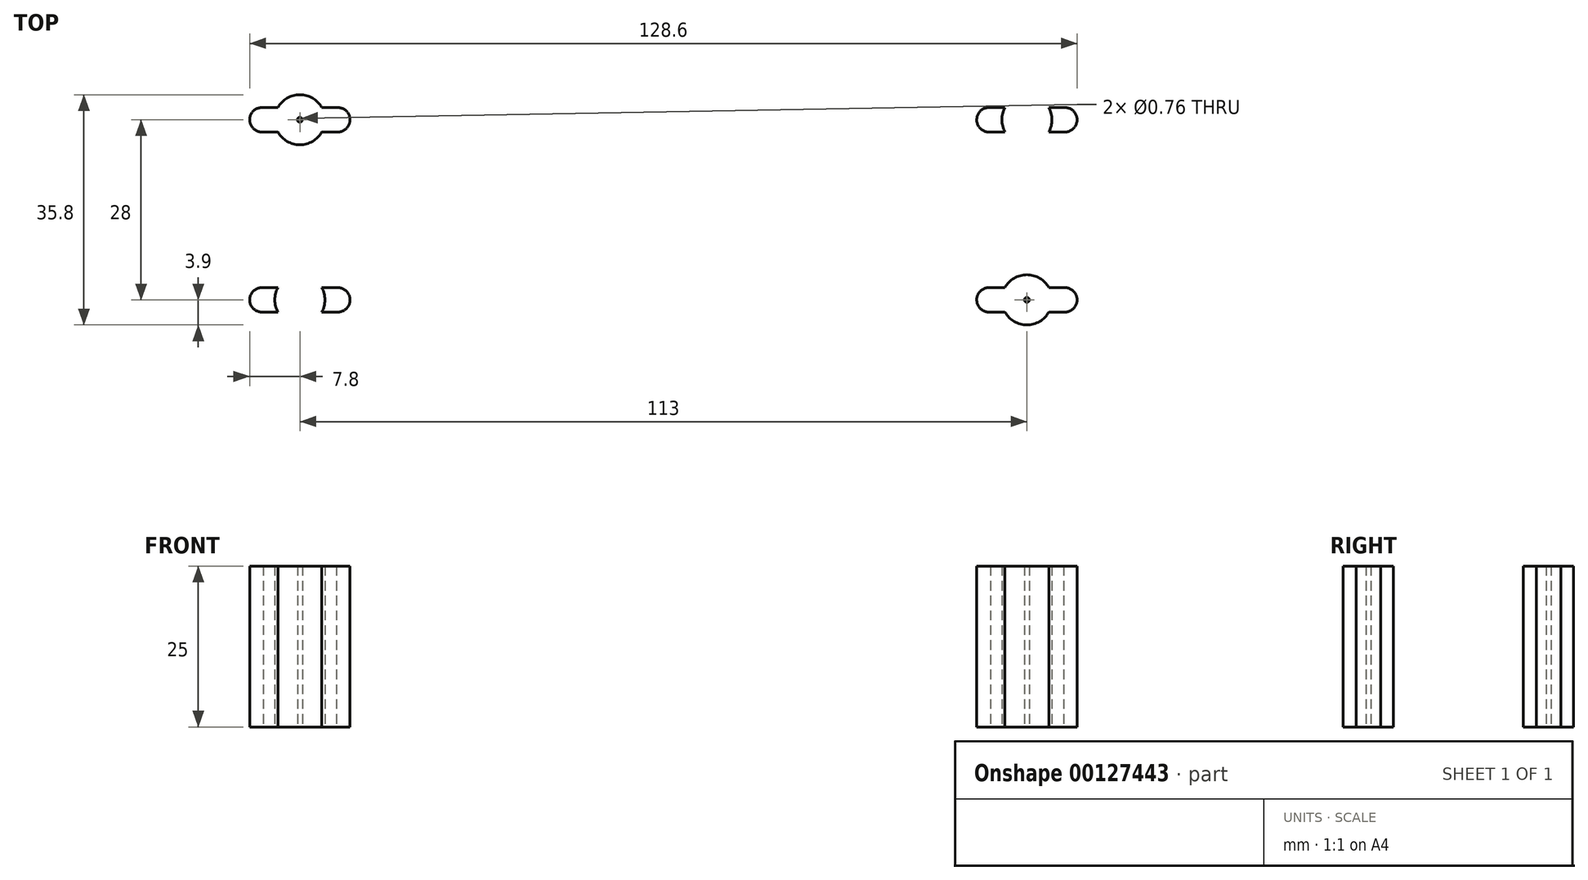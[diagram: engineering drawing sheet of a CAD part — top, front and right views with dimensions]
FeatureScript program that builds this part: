
annotation { "Feature Type Name" : "Feature", "Feature Type Description" : "" }
export const myFeature = defineFeature(function(context is Context, id is Id, definition is map)
    precondition{}
    {
        {
            var Q0;
            Q0=qCreatedBy(makeId("Top.planeOp"),FACE);
            var sketch = newSketch(context, id + "F0", { "sketchPlane" : qUnion([Q0])});
            skLineSegment(sketch, "E0", {"start": v(-53.1, 15.9) * mm, "end": v(-50.6, 15.9) * mm});
            skLineSegment(sketch, "E1", {"start": v(-53.1, 12.1) * mm, "end": v(-50.81, 12.1) * mm});
            skArc(sketch, "E2", {"start": v(-50.6, 15.9) * mm, "mid": v(-48.7, 13.9) * mm, "end": v(-50.81, 12.1) * mm});
            skLineSegment(sketch, "E3", {"start": v(-56.5, 10.1) * mm, "end": v(-56.5, 17.9) * mm, "construction": true});
            skLineSegment(sketch, "E4.MirrorCS", {"start": v(-59.9, 15.9) * mm, "end": v(-62.4, 15.9) * mm});
            skArc(sketch, "E5.MirrorCS", {"start": v(-62.4, 15.9) * mm, "mid": v(-64.3, 13.9) * mm, "end": v(-62.19, 12.1) * mm});
            skLineSegment(sketch, "E6.MirrorCS", {"start": v(-59.9, 12.1) * mm, "end": v(-62.19, 12.1) * mm});
            skArc(sketch, "E7", {"start": v(-59.9, 12.1) * mm, "mid": v(-56.5, 10.1) * mm, "end": v(-53.1, 12.1) * mm});
            skLineSegment(sketch, "E8", {"start": v(0, 35.13) * mm, "end": v(0, -25.28) * mm, "construction": true});
            skLineSegment(sketch, "E9", {"start": v(-57.6, 0) * mm, "end": v(-1, 0) * mm, "construction": true});
            skLineSegment(sketch, "E10.MirrorCS", {"start": v(53.1, 15.9) * mm, "end": v(50.6, 15.9) * mm});
            skLineSegment(sketch, "E11.MirrorCS", {"start": v(53.1, 12.1) * mm, "end": v(50.81, 12.1) * mm});
            skLineSegment(sketch, "E12.MirrorCS", {"start": v(59.9, 12.1) * mm, "end": v(62.19, 12.1) * mm});
            skLineSegment(sketch, "E13.MirrorCS", {"start": v(59.9, 15.9) * mm, "end": v(62.4, 15.9) * mm});
            skArc(sketch, "E14.MirrorCS", {"start": v(50.6, 15.9) * mm, "mid": v(48.7, 13.9) * mm, "end": v(50.81, 12.1) * mm});
            skArc(sketch, "E15.MirrorCS", {"start": v(62.4, 15.9) * mm, "mid": v(64.3, 13.9) * mm, "end": v(62.19, 12.1) * mm});
            skCircle(sketch, "E16.MirrorC", {"center": v(56.5, 14) * mm, "radius": 3.9 * mm});
            skLineSegment(sketch, "E17.MirrorCS", {"start": v(56.5, 10.1) * mm, "end": v(56.5, 17.9) * mm, "construction": true});
            skLineSegment(sketch, "E18.MirrorCS", {"start": v(53.1, -12.1) * mm, "end": v(50.81, -12.1) * mm});
            skLineSegment(sketch, "E19.MirrorCS", {"start": v(53.1, -15.9) * mm, "end": v(50.6, -15.9) * mm});
            skLineSegment(sketch, "E20.MirrorCS", {"start": v(59.9, -12.1) * mm, "end": v(62.19, -12.1) * mm});
            skLineSegment(sketch, "E21.MirrorCS", {"start": v(59.9, -15.9) * mm, "end": v(62.4, -15.9) * mm});
            skLineSegment(sketch, "E22.MirrorCS", {"start": v(-59.9, -12.1) * mm, "end": v(-62.19, -12.1) * mm});
            skCircle(sketch, "E23.MirrorC", {"center": v(56.5, -14) * mm, "radius": 3.9 * mm});
            skLineSegment(sketch, "E24.MirrorCS", {"start": v(-53.1, -12.1) * mm, "end": v(-50.81, -12.1) * mm});
            skLineSegment(sketch, "E25.MirrorCS", {"start": v(56.5, -10.1) * mm, "end": v(56.5, -17.9) * mm, "construction": true});
            skLineSegment(sketch, "E26.MirrorCS", {"start": v(-56.5, -10.1) * mm, "end": v(-56.5, -17.9) * mm, "construction": true});
            skLineSegment(sketch, "E27.MirrorCS", {"start": v(-53.1, -15.9) * mm, "end": v(-50.6, -15.9) * mm});
            skLineSegment(sketch, "E28.MirrorCS", {"start": v(-59.9, -15.9) * mm, "end": v(-62.4, -15.9) * mm});
            skCircle(sketch, "E29.MirrorC", {"center": v(-56.5, -14) * mm, "radius": 3.9 * mm});
            skArc(sketch, "E30.MirrorCS", {"start": v(-50.6, -15.9) * mm, "mid": v(-48.7, -13.9) * mm, "end": v(-50.81, -12.1) * mm});
            skArc(sketch, "E31.MirrorCS", {"start": v(62.4, -15.9) * mm, "mid": v(64.3, -13.9) * mm, "end": v(62.19, -12.1) * mm});
            skArc(sketch, "E32.MirrorCS", {"start": v(-62.4, -15.9) * mm, "mid": v(-64.3, -13.9) * mm, "end": v(-62.19, -12.1) * mm});
            skArc(sketch, "E33.MirrorCS", {"start": v(50.6, -15.9) * mm, "mid": v(48.7, -13.9) * mm, "end": v(50.81, -12.1) * mm});
            skArc(sketch, "E34.trimOffspring", {"start": v(-53.1, 15.9) * mm, "mid": v(-56.5, 17.9) * mm, "end": v(-59.9, 15.9) * mm});
            skCircle(sketch, "E35", {"center": v(-56.5, 14) * mm, "radius": 0.38 * mm});
            skCircle(sketch, "E36.MirrorC", {"center": v(-56.5, -14) * mm, "radius": 0.38 * mm});
            skCircle(sketch, "E37.MirrorC", {"center": v(56.5, 14) * mm, "radius": 0.38 * mm});
            skCircle(sketch, "E38.MirrorC", {"center": v(56.5, -14) * mm, "radius": 0.38 * mm});
            skSolve(sketch);
        }
        {
            var Q0;
            Q0=makeQuery(id+"F0.imprint","IMPRINT",FACE,{"disambiguationData":[TD([[makeQuery(id+"F0.imprint","IMPRINT",EDGE,{"derivedFrom":sQuery(id+"F0.wireOp",EDGE,"E0")}),-1.0]])]});
            var Q1;
            {var subQ0=sQuery(id+"F0.wireOp",EDGE,"E29.MirrorC");var subQ1=makeQuery(id+"F0.imprint","INTERSECT",VERTEX,{"derivedFrom":[sQuery(id+"F0.wireOp",EDGE,"E27.MirrorCS"),subQ0]});Q1=makeQuery(id+"F0.imprint","IMPRINT",FACE,{"disambiguationData":[TD([[makeQuery(id+"F0.imprint","IMPRINT",EDGE,{"disambiguationData":[TD([[subQ1,-1.0]])],"derivedFrom":subQ0}),-1.0]])]});}
            var Q2;
            {var subQ0=sQuery(id+"F0.wireOp",EDGE,"E24.MirrorCS");Q2=makeQuery(id+"F0.imprint","IMPRINT",FACE,{"disambiguationData":[TD([[makeQuery(id+"F0.imprint","IMPRINT",EDGE,{"derivedFrom":subQ0}),-1.0]])]});}
            var Q3;
            {var subQ0=sQuery(id+"F0.wireOp",EDGE,"E22.MirrorCS");Q3=makeQuery(id+"F0.imprint","IMPRINT",FACE,{"disambiguationData":[TD([[makeQuery(id+"F0.imprint","IMPRINT",EDGE,{"derivedFrom":subQ0}),1.0]])]});}
            var Q4;
            {var subQ0=sQuery(id+"F0.wireOp",EDGE,"E18.MirrorCS");Q4=makeQuery(id+"F0.imprint","IMPRINT",FACE,{"disambiguationData":[TD([[makeQuery(id+"F0.imprint","IMPRINT",EDGE,{"derivedFrom":subQ0}),1.0]])]});}
            var Q5;
            {var subQ0=sQuery(id+"F0.wireOp",EDGE,"E23.MirrorC");var subQ1=makeQuery(id+"F0.imprint","INTERSECT",VERTEX,{"derivedFrom":[sQuery(id+"F0.wireOp",EDGE,"E19.MirrorCS"),subQ0]});Q5=makeQuery(id+"F0.imprint","IMPRINT",FACE,{"disambiguationData":[TD([[makeQuery(id+"F0.imprint","IMPRINT",EDGE,{"disambiguationData":[TD([[subQ1,-1.0]])],"derivedFrom":subQ0}),1.0]])]});}
            var Q6;
            {var subQ0=sQuery(id+"F0.wireOp",EDGE,"E20.MirrorCS");Q6=makeQuery(id+"F0.imprint","IMPRINT",FACE,{"disambiguationData":[TD([[makeQuery(id+"F0.imprint","IMPRINT",EDGE,{"derivedFrom":subQ0}),-1.0]])]});}
            var Q7;
            {var subQ0=sQuery(id+"F0.wireOp",EDGE,"E12.MirrorCS");Q7=makeQuery(id+"F0.imprint","IMPRINT",FACE,{"disambiguationData":[TD([[makeQuery(id+"F0.imprint","IMPRINT",EDGE,{"derivedFrom":subQ0}),1.0]])]});}
            var Q8;
            {var subQ0=sQuery(id+"F0.wireOp",EDGE,"E16.MirrorC");var subQ1=makeQuery(id+"F0.imprint","INTERSECT",VERTEX,{"derivedFrom":[sQuery(id+"F0.wireOp",EDGE,"E10.MirrorCS"),subQ0]});Q8=makeQuery(id+"F0.imprint","IMPRINT",FACE,{"disambiguationData":[TD([[makeQuery(id+"F0.imprint","IMPRINT",EDGE,{"disambiguationData":[TD([[subQ1,-1.0]])],"derivedFrom":subQ0}),-1.0]])]});}
            var Q9;
            {var subQ0=sQuery(id+"F0.wireOp",EDGE,"E10.MirrorCS");Q9=makeQuery(id+"F0.imprint","IMPRINT",FACE,{"disambiguationData":[TD([[makeQuery(id+"F0.imprint","IMPRINT",EDGE,{"derivedFrom":subQ0}),1.0]])]});}
            extrude(context, id + "F1", {"entities" : qUnion([Q0, Q1, Q2, Q3, Q4, Q5, Q6, Q7, Q8, Q9]), "depth" : 25 * mm});
        }
    });
